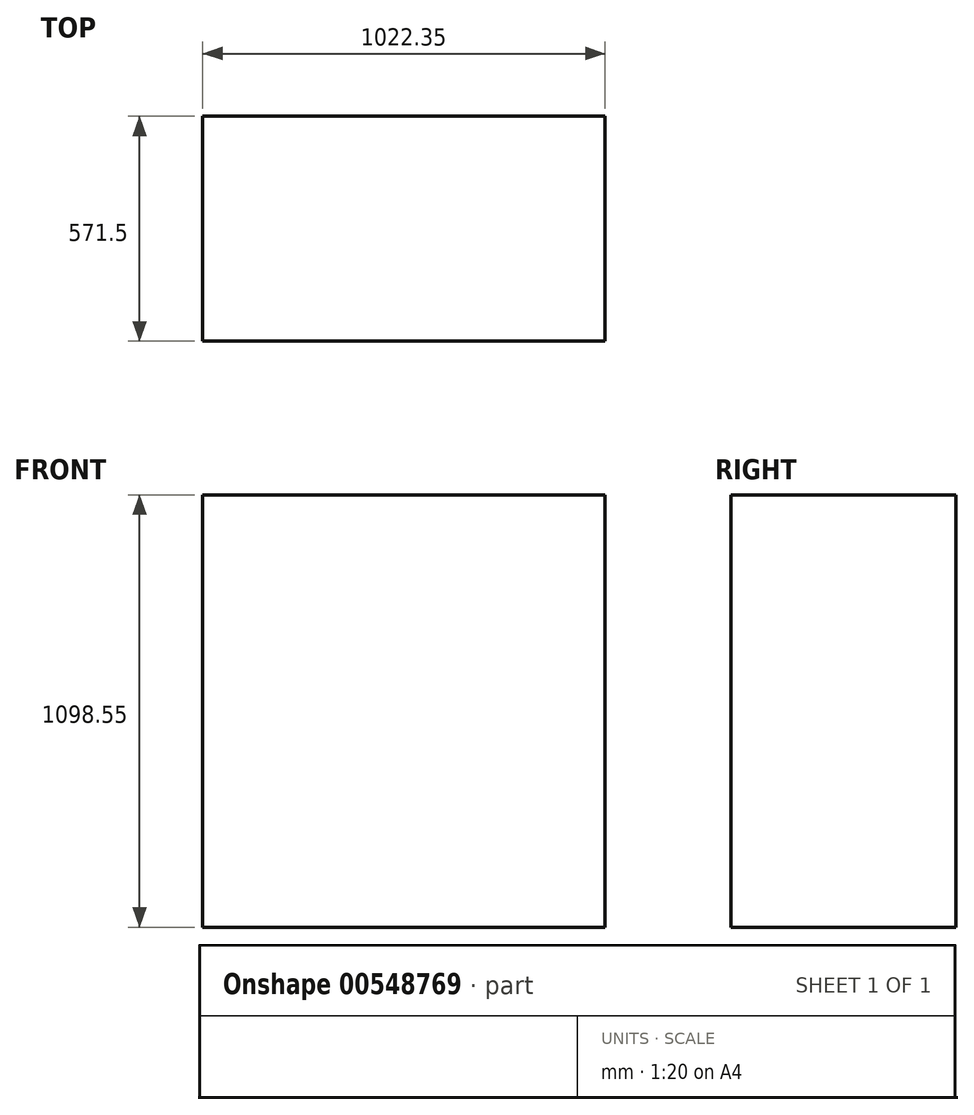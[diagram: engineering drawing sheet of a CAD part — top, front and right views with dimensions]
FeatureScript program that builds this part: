
annotation { "Feature Type Name" : "Feature", "Feature Type Description" : "" }
export const myFeature = defineFeature(function(context is Context, id is Id, definition is map)
    precondition{}
    {
        {
            var Q0;
            Q0=qCreatedBy(makeId("Top.planeOp"),FACE);
            var sketch = newSketch(context, id + "F0", { "sketchPlane" : qUnion([Q0])});
            skLineSegment(sketch, "E0.bottom", {"start": v(0, 0) * mm, "end": v(1022.35, 0) * mm});
            skLineSegment(sketch, "E0.top", {"start": v(0, 571.5) * mm, "end": v(1022.35, 571.5) * mm});
            skLineSegment(sketch, "E0.left", {"start": v(0, 0) * mm, "end": v(0, 571.5) * mm});
            skLineSegment(sketch, "E0.right", {"start": v(1022.35, 0) * mm, "end": v(1022.35, 571.5) * mm});
            skSolve(sketch);
        }
        {
            var Q0;
            Q0 = qSketchRegion(id + "F0", true);
            extrude(context, id + "F1", {"entities" : qUnion([Q0]), "depth" : 1098.55 * mm, "offsetDistance" : 25.4 * mm});
        }
    });
